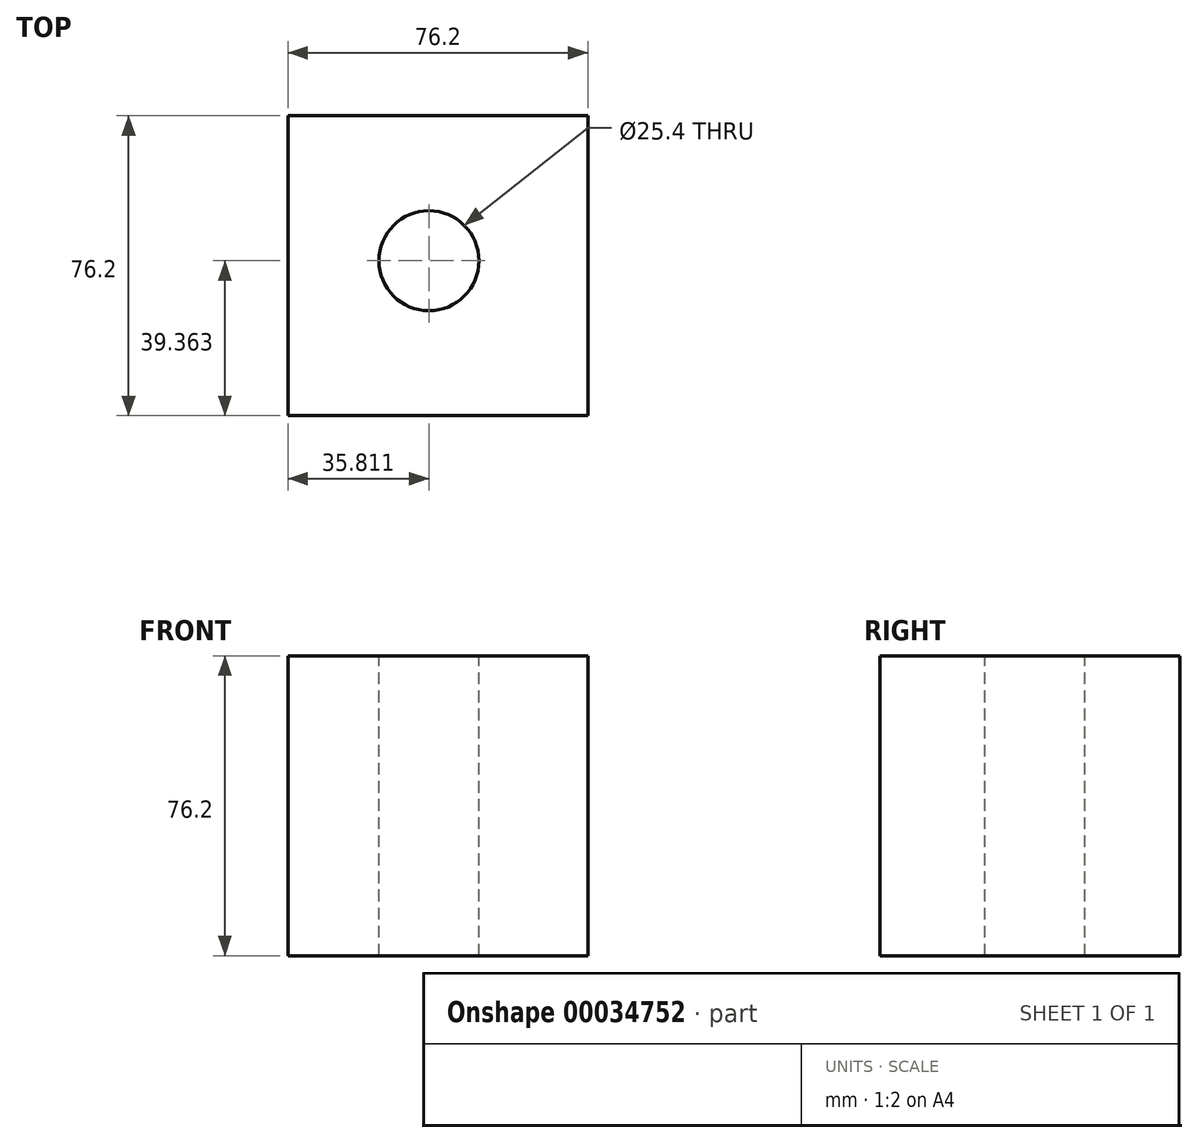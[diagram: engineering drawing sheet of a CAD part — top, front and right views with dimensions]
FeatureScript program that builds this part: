
annotation { "Feature Type Name" : "Feature", "Feature Type Description" : "" }
export const myFeature = defineFeature(function(context is Context, id is Id, definition is map)
    precondition{}
    {
        {
            var Q0;
            Q0=qCreatedBy(makeId("Front.planeOp"),FACE);
            var sketch = newSketch(context, id + "F0", { "sketchPlane" : qUnion([Q0])});
            skLineSegment(sketch, "E0.rect.bottom", {"start": v(38.1, -38.1) * mm, "end": v(-38.1, -38.1) * mm});
            skLineSegment(sketch, "E0.rect.top", {"start": v(38.1, 38.1) * mm, "end": v(-38.1, 38.1) * mm});
            skLineSegment(sketch, "E0.rect.left", {"start": v(38.1, -38.1) * mm, "end": v(38.1, 38.1) * mm});
            skLineSegment(sketch, "E0.rect.right", {"start": v(-38.1, -38.1) * mm, "end": v(-38.1, 38.1) * mm});
            skPoint(sketch, "E0.rect.middle", {"position": v(0, 0) * mm});
            skSolve(sketch);
        }
        {
            var Q0;
            Q0=makeQuery(id+"F0.imprint","IMPRINT",FACE,{"disambiguationData":[TD([[makeQuery(id+"F0.imprint","IMPRINT",EDGE,{"derivedFrom":sQuery(id+"F0.wireOp",EDGE,"E0.rect.bottom")}),-1.0]])]});
            extrude(context, id + "F1", {"entities" : qUnion([Q0]), "depth" : 76.2 * mm});
        }
        {
            var Q0;
            Q0=makeQuery(id+"F1.opExtrude","SWEPT_FACE",FACE,{"disambiguationData":[OSD([sQuery(id+"F0.wireOp",EDGE,"E0.rect.top")])]});
            var sketch = newSketch(context, id + "F2", { "sketchPlane" : qUnion([Q0])});
            skCircle(sketch, "E1", {"center": v(-2.29, -36.84) * mm, "radius": 25.4 * mm});
            skSolve(sketch);
        }
        {
            var Q0;
            Q0=sQuery(id+"F2.wireOp",VERTEX,"E1.center");
            var Q1;
            Q1=makeQuery(id+"F1.opExtrude","SWEPT_BODY",BODY,{"disambiguationData":[OSD([sQuery(id+"F0.wireOp",EDGE,"E0.rect.bottom"),sQuery(id+"F0.wireOp",EDGE,"E0.rect.top"),sQuery(id+"F0.wireOp",EDGE,"E0.rect.left"),sQuery(id+"F0.wireOp",EDGE,"E0.rect.right")])]});
            hole(context, id + "F3", {"style" : HoleStyle.SIMPLE, "holeDiameter" : 25.4 * mm, "endStyle" : HoleEndStyle.THROUGH, "locations" : qUnion([Q0]), "scope" : qUnion([Q1])});
        }
    });
